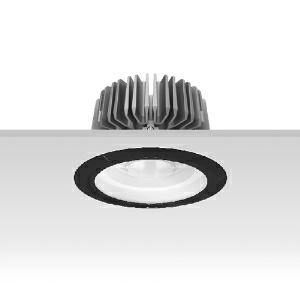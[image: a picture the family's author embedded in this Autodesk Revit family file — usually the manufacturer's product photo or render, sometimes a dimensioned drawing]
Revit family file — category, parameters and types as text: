
# Revit family: 3f_filippi_-_3f_reno_bianco_ampio_3f_filippi_-_30362_a01024_-_3f_reno_150_wh_2000-930_ep_wide___vt_bk_621f
name_source: partatom
category: Lighting Fixtures
units: mm (PartAtom-declared; Revit-internal decimal feet)

## family parameters
Cut with Voids When Loaded = No
Host = Face
Light Source = No
Part Type = Normal
Room Calculation Point = No
Round Connector Dimension = Use Diameter
Shared = No

## types (1)
- 3F Filippi - 3F Reno Bianco Ampio (1 x LED, 1888 lm, 25 W, 3000 K)
    Apparent Load = 25 VA
    Approval mark = ENEC
    CIE Flux Codes = 74 93 99 100 100
    Color Rendering = 90
    Color Temperature = 3000 K
    Control Gear = Electronic ballast
    Default Elevation = 1800 mm
    Description = ILLUMINOTECHNICAL
Luminous efficiency 100% (DLOR 100%, ULOR 0%).
Initial luminous flux of the luminaire 1888 lm.
Emergency luminaire luminous flux BLF 16.7%.
Direct symmetric wide distribution.
Installation Interdistance Transv.D = 1.54 x hu - Long.D = 1.54 x hu.
Tabular UGR (CIE 117 - 4H-8H; S=0.25H; 70/50/20): RUG 23.2 - 23.
Beam angle: 74° - 73°.
Luminous efficacy 76 lm/W.
Lifetime (L90/B10): 30000 h. (tq+25°C)
Lifetime (L85/B10): 50000 h. (tq+25°C)
Lifetime (L70/B10): 80000 h. (tq+25°C)
Sudden decreased luminous flux after 50000 hours: 0% (C0).
Photobiological safety in compliance with IEC/TR 62778: RG0 risk exempt, (IEC 62471).
In compliance with IEC/EN 62722-2-1 - IEC/EN 62717 standards.

SOURCE
Compact LED module 2000/930.
Energy efficiency class (UE 2019/2020 - UE 2019/2015): E.
CIE 13.3 Colour rendering index: CRI >90 (R9 >50%).
IES TM-30 Fidelity Index: Rf = 92 Rg = 101.
CCT nominal colour temperature 3000 K.
Colour initial tolerance (MacAdam): SDCM 3.
Zhaga Book 3 compliant.

MECHANICAL
Passive heat dissipator in die-casting aluminium, oversized, for optimum thermal management of the LED module.
Parabolic element with graduated/concentric rings in white polycarbonate.
Transparent external lens with glossy and satin differentiated surfaces, with a cooling and anti-insect system in methacrylate (PMMA).
Fastening spring clips in stainless steel.
Dimensions: diameter 176 mm, height 111 mm. Weight 1.35 kg.
IP44 protection degree for exposed part, IP20 for recessed part.
Mechanical strength to impacts IK06 (1 joule).
Glow-wire test resistance 650°C.

ELECTRICAL
Wiring on a separate unit.
Halogen Free electronic wiring 230V-50/60Hz, power factor 0.90, THD <25%, constant output current, SELV, class II, 1 driver.
Power of the luminaire 25 W.
CE - IEC 60598-1 - EN 60598-1.
EP maintained emergency wiring on board, 1h duration, 24h recharge; compliant with EN 60598-2-22, excluding high risk areas.
SAFE FLICKER: PstLM=<1 and SVM=<0.4 (IEC TR 61547-1 and IEC TR 63158), to ensure a more comfortable and safe light.
Ambient temperature from +5°C to +25°C.
Temperature class T6 max 85°C.
Relative humidity UR: <85%.

INSTALLATION
Pull-up recessed fitting.
False ceiling carving: 150 mm.
All accessories dedicated to this product are available on the Catalog and on our website www.3F-Filippi.com.

ACCESSORIES
A01024 - VT transparent glass, tempered, not flammable, locked and in line with the trim, in black polycarbonate.

APPLICATIONS
Environments: architectural, commercial, exhibition areas, transit areas, corridors, shops, display windows, service areas.
In false ceilings with narrow voids.

WARNING
Luminaire designed for disposal/recycling at end-of-life.
Replaceable (LED only) light source by a professional. Replaceable control gear by a professional.
    Height = 0 mm  [stored 0 ft]
    Lamp = 1 x LED
    Lamp Light Flux = 1888 lm
    Lamp Power = 25 W
    Lamp count = 1
    Length = 176 mm
    Lifetime = 50000 h
    Luminous efficacy = 76 lm/W
    Manufacturer = 3F Filippi
    ModVariant = No
    Model = 3F Filippi - 30362+A01024 - 3F Reno 150 WH 2000-930 EP WIDE + VT BK
    Mounting Place = Ceiling
    Mounting Type = Recessed
    Number of Poles = 1
    OnlyDefault = Yes
    Power Factor = 1
    Product Name = 3F Filippi - 3F Reno Bianco Ampio
    Product group = recessed luminaire
    ProductGroupID = 4
    Protection Class = Protection class II
    Protection Degree = IP 20
    RLX_Detail_Level = 1
    RLX_Emergency_Light_Flux = 0 lm
    RLX_Emergency_Type = 0
    RLX_Emergency_Type_DB = No
    RlxData = <blob elided: 88505 chars, md5=5476c383>
    Socket = socket
    Standby Power = 0 W
    System Light Flux = 1888 lm
    System Power = 25 W
    Type Comments = Product without accessories
    Type Image = 3ffilippi_3f_reno_150_wh_d150__a01024.jpg
    URL = http://relux.com
    VarID = ---
    Voltage = 0 V
    Weight = 0.00 kg
    Width = 0 mm  [stored 0 ft]

note: [stored X ft] marks values corroborated as IEEE doubles in the binary element streams (Revit-internal decimal feet)

## geometry (parser evidence)
native form markers: Blend x4, Sweep x12
no freeform markers — native parametric forms only
